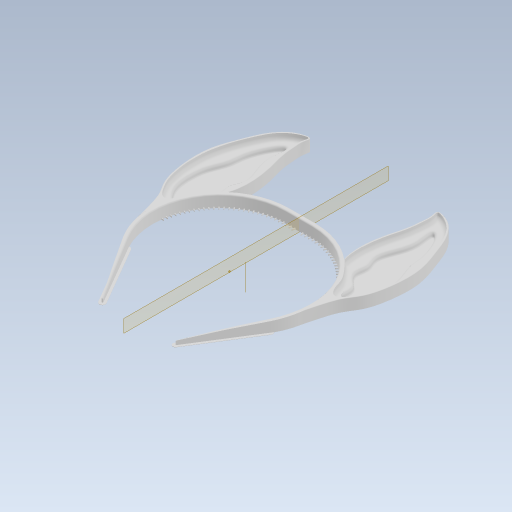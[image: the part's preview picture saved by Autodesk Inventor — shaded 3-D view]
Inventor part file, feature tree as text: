
AUTODESK INVENTOR PART (.ipt)
format: ipt  version: 2023 (Build 270158030, 158C)  size: 2,766,848 bytes
history: native  units: in
note: dims shown in document units (in); Inventor stores cm internally (conversion verified against a paired STEP export)
features: fillet x19, extrude x13, sketch x12, projected_geometry x7, other x1, pattern_circular x1, mirror x1, chamfer x1
ambient origin geometry x8: Origin, YZ Plane, XZ Plane, XY Plane, X Axis, Y Axis, Z Axis, Center Point
bodies: Solid1 (feature_tree), Solid2 (feature_tree)
feature tree (55):
  extrude  "Extrusion1"  Depth=2.2638in
  extrude  "Extrusion2"  Depth=0.3937in TaperAngle=0.0deg
  fillet  "Fillet2"  Radius=0.0433in
  other  "Work Axis1"
  pattern_circular  "Circular Pattern1"  Count=30  [1 undecoded]
  extrude  "Extrusion4"  Depth=4.3307in
  fillet  "Fillet6"  Radius=25.1969in
  fillet  "Fillet7"  Radius=0.7087in
  fillet  "Fillet8"  Radius=4.3307in
  extrude  "Extrusion10"  TaperAngle=0.0deg  [1 undecoded]
  extrude  "Extrusion11"  Depth=0.0394in
  extrude  "Extrusion12"  Depth=0.3937in TaperAngle=0.0deg
  fillet  "Fillet32"  Radius=0.315in
  fillet  "Fillet33"  Radius=0.0591in
  fillet  "Fillet35"  Radius=0.0591in
  fillet  "Fillet36"  Radius=1.378in
  extrude  "Extrusion13"  Depth=2.3495in
  mirror  "Mirror1"
  extrude  "Extrusion14"  Depth=2.0826in
  fillet  "Fillet30"  Radius=1.4138in
  fillet  "Fillet28"  Radius=2.5284in
  fillet  "Fillet19"  Radius=1.4901in
  extrude  "Extrusion5"  Depth=2.5146in
  extrude  "Extrusion7"  Depth=0.0079in
  extrude  "Extrusion6"  Depth=0.0079in
  fillet  "Fillet20"  Radius=0.3104in
  fillet  "Fillet21"  Radius=0.2859in
  fillet  "Fillet22"  Radius=0.2088in
  fillet  "Fillet23"  Radius=0.2171in
  fillet  "Fillet24"  Radius=0.23in
  fillet  "Fillet25"  Radius=0.2362in
  fillet  "Fillet26"  Radius=0.0787in
  extrude  "Extrusion8"  Depth=0.0079in
  fillet  "Fillet27"  Radius=0.0394in
  extrude  "Extrusion9"  Depth=0.0079in
  chamfer  "Chamfer1"  Distance=0.1181in
  sketch  "Sketch1"  dims[d23=2.2638in d25=0.1181in]
  sketch  "Sketch2"  dims[d27=0.1181in d30=0.3937in d31=0.0in d48=0.0433in d49=0.0in]
  sketch  "Sketch7"  dims[d50=0.0118in]
  sketch  "Sketch8"  dims[d57=0.0787in d58=0.0157in d61=11.811in d62=-0.6184in]
  sketch  "Sketch9"  dims[d65=3.1496in d76=4.3307in d77=25.1969in d78=0.7087in d79=4.3307in]
  sketch  "Sketch11"  dims[d80=0.3937in d81=0.0in d82=0.0in]
  sketch  "Sketch12"  dims[d86=0.0394in d87=0.0394in]
  projected_geometry  "Projected Loop1"
  sketch  "Sketch13"  dims[d88=0.0236in d104=0.3937in d105=0.0in d107=0.315in d108=0.0in d121=0.0591in d122=0.0591in d123=1.378in]
  projected_geometry  "Projected Loop2"
  projected_geometry  "Projected Loop3"
  sketch  "Sketch14"  dims[d125=0.3346in d126=0.0in d130=2.3495in]
  projected_geometry  "Projected Loop4"
  sketch  "Sketch16"  dims[d131=2.2052in d132=2.0826in d133=1.4138in d134=2.5284in d135=1.4901in]
  projected_geometry  "Projected Loop5"
  sketch  "Sketch18"  dims[d136=2.1896in d137=2.5146in]
  projected_geometry  "Projected Loop6"
  sketch  "Sketch19"  dims[d138=2.7368in d139=1.4623in d140=0.488in d141=0.3104in d142=0.2859in d143=0.2088in d144=0.2171in d145=0.23in d147=0.2362in d148=0.0787in d149=0.0787in d150=0.0394in d153=0.0394in d154=0.1181in d155=0.0787in d156=0.0787in d158=23.622in d159=1.9685in d161=7.8078in d162=2.3622in d163=0.7874in d164=0.9817in d165=0.0in d167=0.0787in d168=0.1969in d169=0.1969in d170=0.1181in d171=0.0197in d172=0.0079in d173=0.0394in d174=0.0197in d175=0.0197in d182=0.0984in d183=0.0394in d184=0.0984in d185=0.0394in d186=0.0591in d187=0.0394in d188=0.0197in d189=0.076in d190=0.0in d191=0.0in d192=0.0079in d193=0.0197in d194=0.0787in d195=45.0deg d196=0.0in d197=0.0in d199=0.3937in d200=0.0in d201=0.3543in d202=0.0in d203=0.315in d205=0.1969in d206=0.0in d207=0.1181in d209=0.0118in d210=0.1181in d212=0.0394in d216=0.7874in d217=0.4331in d218=2.3622in d219=0.4331in d220=0.0984in d221=0.3937in d222=0.1181in d223=0.0787in d224=0.1969in d225=0.0in d226=0.0787in d227=0.2047in d228=0.0787in d229=0.0079in d230=0.0in]
  projected_geometry  "Projected Loop7"
note: 2 required parameter values undecoded (feature->parameter linkage not recoverable at this tier; creation-order binding heuristic only, values carry confidence <= 0.55)
